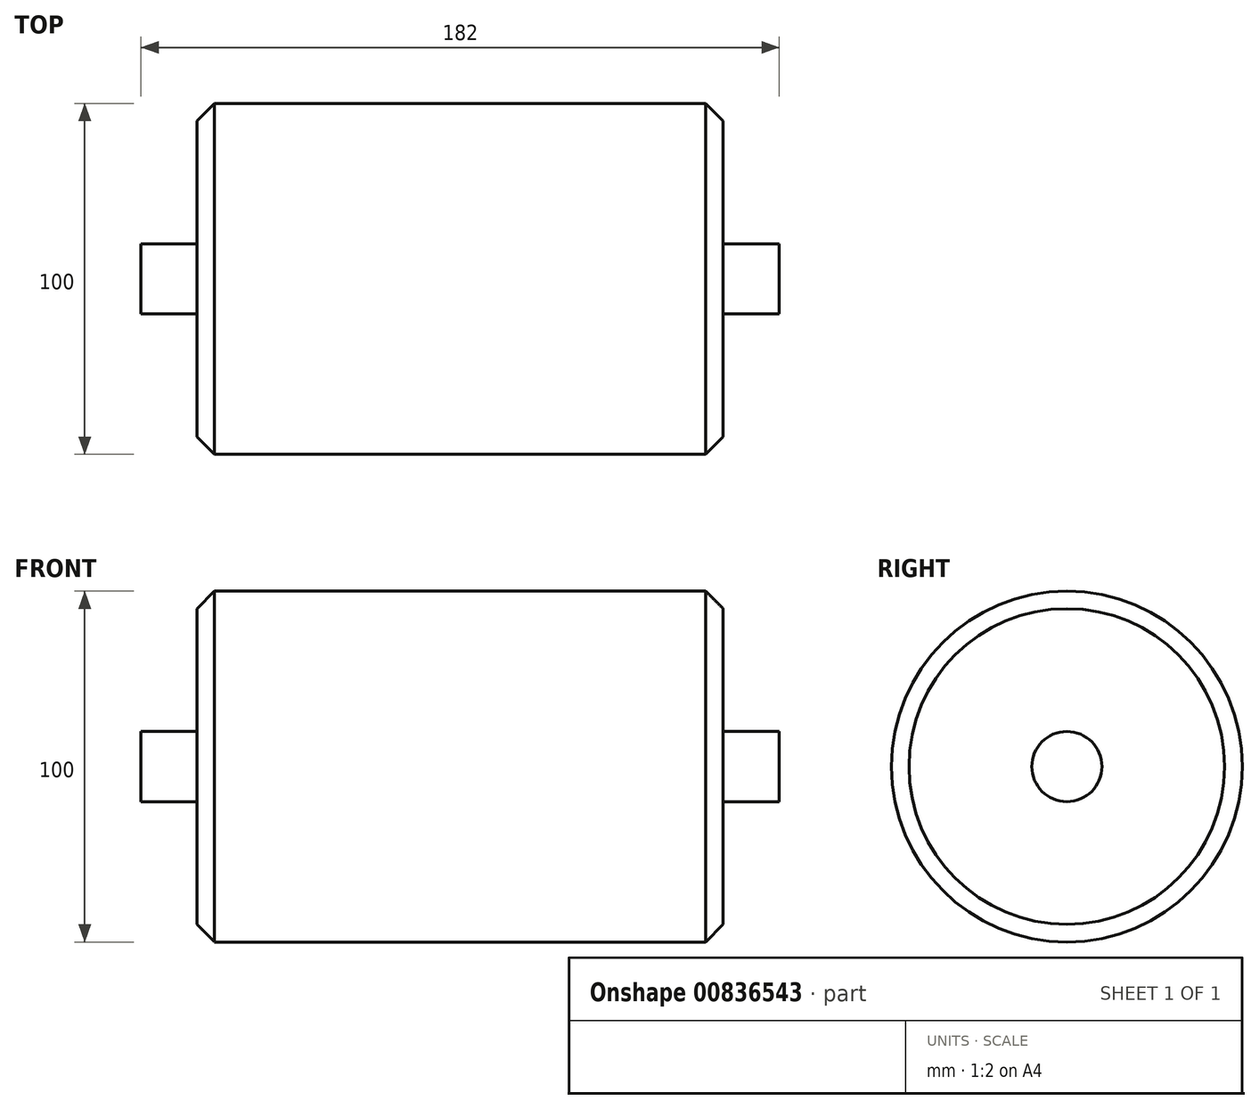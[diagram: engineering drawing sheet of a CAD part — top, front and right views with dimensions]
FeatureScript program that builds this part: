
annotation { "Feature Type Name" : "Feature", "Feature Type Description" : "" }
export const myFeature = defineFeature(function(context is Context, id is Id, definition is map)
    precondition{}
    {
        {
            var Q0;
            Q0=qCreatedBy(makeId("Top.planeOp"),FACE);
            var sketch = newSketch(context, id + "F0", { "sketchPlane" : qUnion([Q0])});
            skLineSegment(sketch, "E0", {"start": v(-91, 0) * mm, "end": v(-91, 10) * mm});
            skLineSegment(sketch, "E1", {"start": v(-91, 10) * mm, "end": v(-75, 10) * mm});
            skLineSegment(sketch, "E2", {"start": v(-75, 10) * mm, "end": v(-75, 50) * mm});
            skLineSegment(sketch, "E3", {"start": v(-75, 50) * mm, "end": v(75, 50) * mm});
            skLineSegment(sketch, "E4", {"start": v(75, 50) * mm, "end": v(75, 10) * mm});
            skLineSegment(sketch, "E5", {"start": v(75, 10) * mm, "end": v(91, 10) * mm});
            skLineSegment(sketch, "E6", {"start": v(91, 10) * mm, "end": v(91, 0) * mm});
            skLineSegment(sketch, "E7", {"start": v(91, 0) * mm, "end": v(-91, 0) * mm});
            skSolve(sketch);
        }
        {
            var Q0;
            Q0 = qSketchRegion(id + "F0", true);
            var Q1;
            Q1=sQuery(id+"F0.wireOp",EDGE,"E7");
            revolve(context, id + "F1", {"surfaceOperationType" : NewSurfaceOperationType.NEW, "entities" : qUnion([Q0]), "axis" : qUnion([Q1]), "revolveType" : RevolveType.FULL});
        }
        {
            var Q0;
            Q0=makeQuery(id+"F1.opRevolve","SWEPT_EDGE",EDGE,{"disambiguationData":[OSD([sQuery(id+"F0.wireOp",EDGE,"E3"),sQuery(id+"F0.wireOp",EDGE,"E4")])]});
            chamfer(context, id + "F2", {"entities" : qUnion([Q0]), "chamferType" : ChamferType.OFFSET_ANGLE, "width" : 5 * mm, "oppositeDirection" : false, "angle" : 45 * degree, "tangentPropagation" : true});
        }
        {
            var Q0;
            Q0=makeQuery(id+"F1.opRevolve","SWEPT_EDGE",EDGE,{"disambiguationData":[OSD([sQuery(id+"F0.wireOp",EDGE,"E2"),sQuery(id+"F0.wireOp",EDGE,"E3")])]});
            chamfer(context, id + "F3", {"entities" : qUnion([Q0]), "chamferType" : ChamferType.OFFSET_ANGLE, "width" : 5 * mm, "oppositeDirection" : false, "angle" : 45 * degree, "tangentPropagation" : true});
        }
    });
